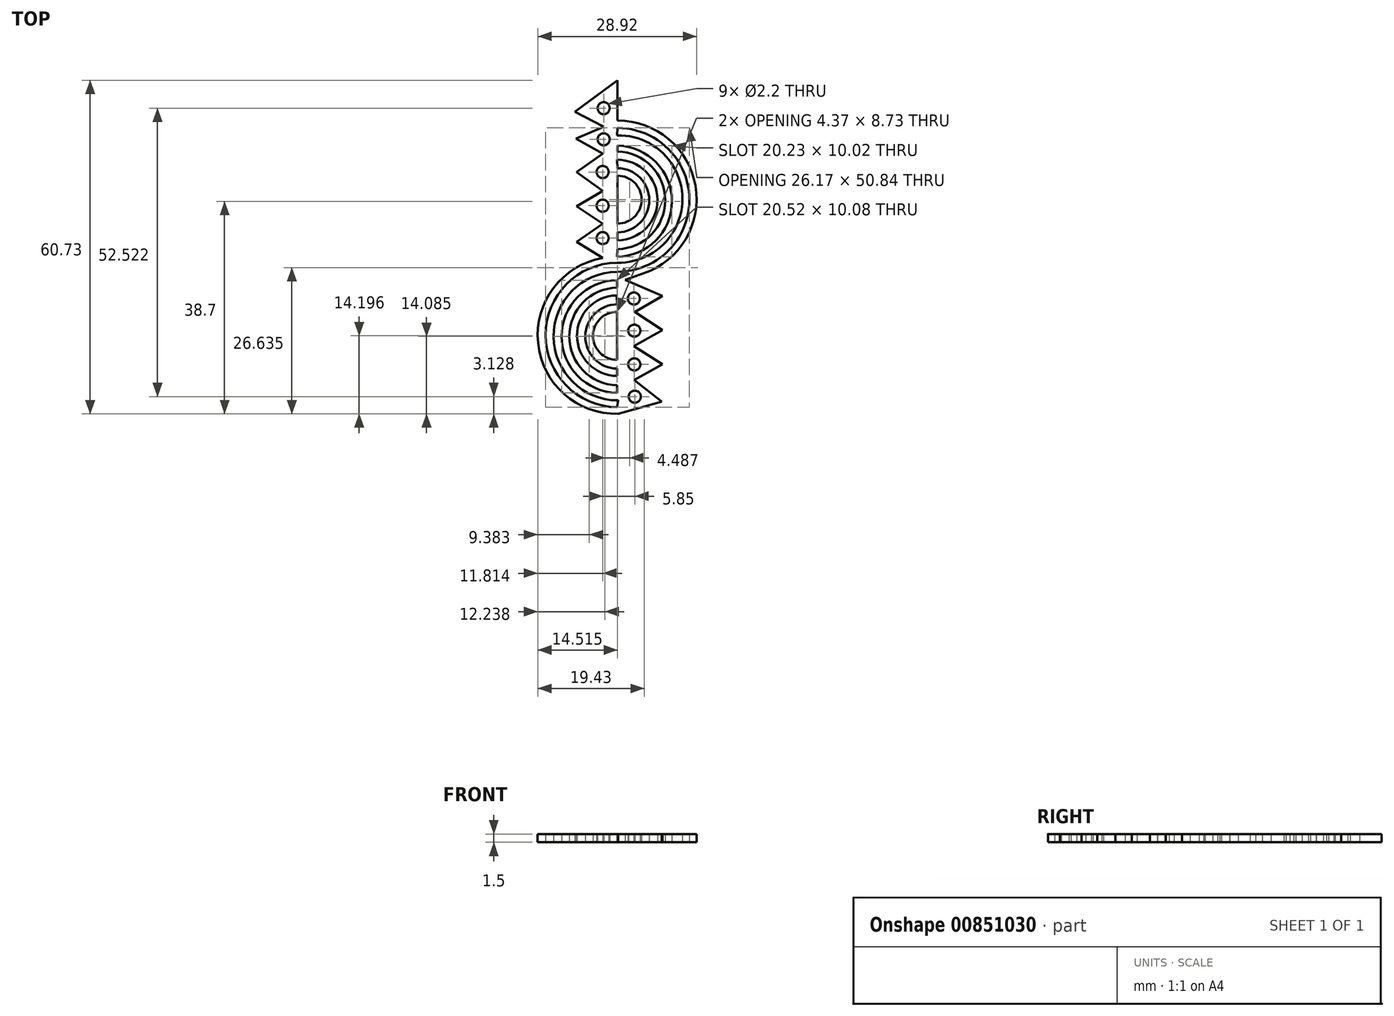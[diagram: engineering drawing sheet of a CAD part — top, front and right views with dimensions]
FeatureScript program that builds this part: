
annotation { "Feature Type Name" : "Feature", "Feature Type Description" : "" }
export const myFeature = defineFeature(function(context is Context, id is Id, definition is map)
    precondition{}
    {
        {
            var Q0;
            Q0=qCreatedBy(makeId("Top.planeOp"),FACE);
            var sketch = newSketch(context, id + "F0", { "sketchPlane" : qUnion([Q0])});
            skLineSegment(sketch, "E0", {"start": v(-35.28, 27.67) * mm, "end": v(-1.98, 27.67) * mm, "construction": true});
            skArc(sketch, "E1", {"start": v(-17.96, 29.75) * mm, "mid": v(-7.94, 39.81) * mm, "end": v(-17.84, 49.99) * mm});
            skArc(sketch, "E2", {"start": v(-17.84, 35.8) * mm, "mid": v(-13.47, 40.16) * mm, "end": v(-17.84, 44.53) * mm});
            skArc(sketch, "E3", {"start": v(-13.09, 26.74) * mm, "mid": v(-3.67, 42.66) * mm, "end": v(-17.84, 54.55) * mm});
            skArc(sketch, "E4", {"start": v(-17.84, 31.17) * mm, "mid": v(-9.16, 40.05) * mm, "end": v(-17.84, 48.92) * mm});
            skArc(sketch, "E5", {"start": v(-17.84, 34.2) * mm, "mid": v(-12.08, 40.05) * mm, "end": v(-17.84, 45.9) * mm});
            skLineSegment(sketch, "E6", {"start": v(-20.37, 53.46) * mm, "end": v(-25.44, 51.28) * mm});
            skLineSegment(sketch, "E7", {"start": v(-25.44, 51.28) * mm, "end": v(-20.57, 48.55) * mm});
            skLineSegment(sketch, "E8", {"start": v(-20.57, 48.55) * mm, "end": v(-25.28, 45.18) * mm});
            skLineSegment(sketch, "E9", {"start": v(-25.28, 45.18) * mm, "end": v(-20.57, 41.77) * mm});
            skLineSegment(sketch, "E10", {"start": v(-20.57, 41.77) * mm, "end": v(-25.28, 38.98) * mm});
            skLineSegment(sketch, "E11", {"start": v(-25.28, 38.98) * mm, "end": v(-20.57, 35.78) * mm});
            skLineSegment(sketch, "E12", {"start": v(-20.57, 35.78) * mm, "end": v(-25.28, 32.45) * mm});
            skLineSegment(sketch, "E13", {"start": v(-25.28, 32.45) * mm, "end": v(-20.57, 29.54) * mm});
            skLineSegment(sketch, "E14", {"start": v(-17.84, 49.99) * mm, "end": v(-17.84, 48.92) * mm});
            skLineSegment(sketch, "E15.MirrorCS", {"start": v(-9.67, 22.6) * mm, "end": v(-14.72, 19.72) * mm});
            skArc(sketch, "E16.MirrorCS", {"start": v(-17.96, 6.38) * mm, "mid": v(-26.64, 15.26) * mm, "end": v(-17.96, 24.13) * mm});
            skArc(sketch, "E17.MirrorCS", {"start": v(-17.74, 1.17) * mm, "mid": v(-32.31, 14.05) * mm, "end": v(-20.57, 29.54) * mm});
            skLineSegment(sketch, "E18.MirrorCS", {"start": v(-14.8, 7.3) * mm, "end": v(-9.83, 3.38) * mm});
            skLineSegment(sketch, "E19.MirrorCS", {"start": v(-16.45, 25.58) * mm, "end": v(-9.67, 22.6) * mm});
            skLineSegment(sketch, "E20.MirrorCS", {"start": v(-14.72, 19.72) * mm, "end": v(-9.67, 16.42) * mm});
            skLineSegment(sketch, "E21.MirrorCS", {"start": v(-9.67, 16.42) * mm, "end": v(-14.9, 13.46) * mm});
            skArc(sketch, "E22.MirrorCS", {"start": v(-17.96, 11) * mm, "mid": v(-22.33, 15.37) * mm, "end": v(-17.96, 19.73) * mm});
            skLineSegment(sketch, "E23.MirrorCS", {"start": v(-9.67, 10.16) * mm, "end": v(-14.8, 7.3) * mm});
            skArc(sketch, "E24.MirrorCS", {"start": v(-17.96, 5) * mm, "mid": v(-28.03, 15.26) * mm, "end": v(-17.96, 25.51) * mm});
            skLineSegment(sketch, "E25.MirrorCS", {"start": v(-17.96, 25.51) * mm, "end": v(-17.96, 24.13) * mm});
            skLineSegment(sketch, "E26.MirrorCS", {"start": v(-17.96, 6.38) * mm, "end": v(-17.96, 5) * mm});
            skArc(sketch, "E27.MirrorCS", {"start": v(-17.96, 9.4) * mm, "mid": v(-23.72, 15.26) * mm, "end": v(-17.96, 21.11) * mm});
            skLineSegment(sketch, "E28.MirrorCS", {"start": v(-14.9, 13.46) * mm, "end": v(-9.67, 10.16) * mm});
            skLineSegment(sketch, "E29.MirrorCS", {"start": v(-9.83, 3.38) * mm, "end": v(-17.74, 1.17) * mm});
            skLineSegment(sketch, "E30.trimOffspring", {"start": v(-17.84, 48.92) * mm, "end": v(-17.84, 49.99) * mm, "construction": true});
            skLineSegment(sketch, "E31.trimOffspring", {"start": v(-17.84, 54.55) * mm, "end": v(-17.84, 58.38) * mm, "construction": true});
            skLineSegment(sketch, "E32.trimOffspring", {"start": v(-17.84, 44.53) * mm, "end": v(-17.84, 45.9) * mm, "construction": true});
            skLineSegment(sketch, "E33", {"start": v(-16.45, 25.58) * mm, "end": v(-13.09, 26.74) * mm});
            skLineSegment(sketch, "E34", {"start": v(-17.96, 29.75) * mm, "end": v(-17.84, 31.17) * mm});
            skArc(sketch, "E35", {"start": v(-17.96, 27.03) * mm, "mid": v(-4.78, 40.07) * mm, "end": v(-17.84, 53.22) * mm});
            skArc(sketch, "E36", {"start": v(-17.96, 28.69) * mm, "mid": v(-6.04, 40.27) * mm, "end": v(-17.96, 51.86) * mm});
            skArc(sketch, "E37", {"start": v(-17.96, 27.03) * mm, "mid": v(-29.5, 15.22) * mm, "end": v(-17.75, 3.62) * mm});
            skArc(sketch, "E38", {"start": v(-17.96, 28.69) * mm, "mid": v(-30.95, 15.54) * mm, "end": v(-17.96, 2.39) * mm});
            skLineSegment(sketch, "E39", {"start": v(-17.96, 2.39) * mm, "end": v(-17.75, 3.62) * mm});
            skArc(sketch, "E40", {"start": v(-18.01, 22.72) * mm, "mid": v(-25.22, 15.37) * mm, "end": v(-17.96, 8.07) * mm});
            skCircle(sketch, "E41", {"center": v(-20.37, 51.15) * mm, "radius": 1.1 * mm});
            skCircle(sketch, "E42", {"center": v(-20.57, 45.2) * mm, "radius": 1.1 * mm});
            skCircle(sketch, "E43", {"center": v(-20.57, 39.06) * mm, "radius": 1.1 * mm});
            skCircle(sketch, "E44", {"center": v(-20.57, 33.16) * mm, "radius": 1.1 * mm});
            skCircle(sketch, "E45", {"center": v(-14.87, 22.16) * mm, "radius": 1.1 * mm});
            skCircle(sketch, "E46", {"center": v(-14.8, 16.31) * mm, "radius": 1.1 * mm});
            skCircle(sketch, "E47", {"center": v(-14.8, 10.17) * mm, "radius": 1.1 * mm});
            skCircle(sketch, "E48", {"center": v(-14.72, 4.3) * mm, "radius": 1.1 * mm});
            skLineSegment(sketch, "E49", {"start": v(-17.84, 53.22) * mm, "end": v(-17.96, 51.86) * mm});
            skLineSegment(sketch, "E50", {"start": v(-20.37, 53.46) * mm, "end": v(-25.63, 56.17) * mm});
            skLineSegment(sketch, "E51", {"start": v(-25.63, 56.17) * mm, "end": v(-17.84, 61.9) * mm});
            skLineSegment(sketch, "E52", {"start": v(-17.84, 61.9) * mm, "end": v(-17.84, 54.55) * mm});
            skCircle(sketch, "E53", {"center": v(-20.37, 56.82) * mm, "radius": 1.1 * mm});
            skLineSegment(sketch, "E54", {"start": v(-17.96, 21.11) * mm, "end": v(-18.01, 22.72) * mm});
            skLineSegment(sketch, "E55", {"start": v(-17.96, 9.4) * mm, "end": v(-17.96, 8.07) * mm});
            skLineSegment(sketch, "E56", {"start": v(-17.96, 19.73) * mm, "end": v(-17.96, 11) * mm});
            skArc(sketch, "E57", {"start": v(-17.84, 32.74) * mm, "mid": v(-10.57, 40.13) * mm, "end": v(-17.92, 47.44) * mm});
            skLineSegment(sketch, "E58", {"start": v(-17.84, 44.53) * mm, "end": v(-17.84, 35.8) * mm});
            skLineSegment(sketch, "E59", {"start": v(-17.84, 45.9) * mm, "end": v(-17.92, 47.44) * mm});
            skLineSegment(sketch, "E60", {"start": v(-17.84, 34.2) * mm, "end": v(-17.84, 32.74) * mm});
            skPoint(sketch, "E61.orphan", {"position": v(-9.67, 28.47) * mm});
            skSolve(sketch);
        }
        {
            var Q0;
            Q0 = qSketchRegion(id + "F0", true);
            extrude(context, id + "F1", {"entities" : qUnion([Q0]), "depth" : 1.5 * mm, "offsetDistance" : 25 * mm});
        }
    });
